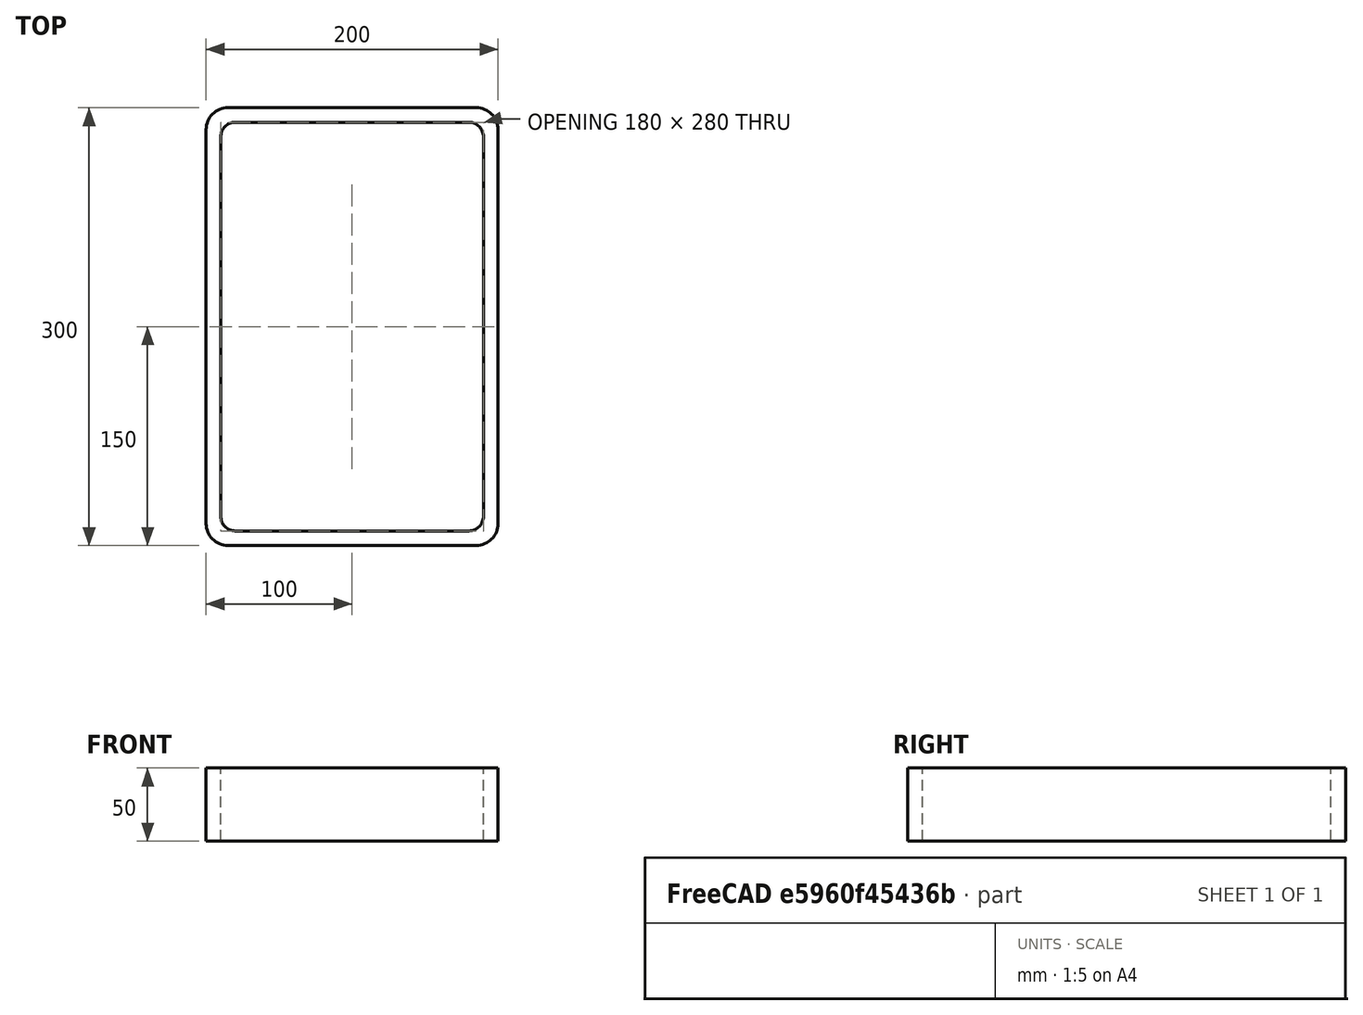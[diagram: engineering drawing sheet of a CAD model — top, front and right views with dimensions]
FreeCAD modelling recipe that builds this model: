
FCSTD DOCUMENT  (FreeCAD 0.15R4671 (Git))
Label: Rectangular hollow section 300x200x10 EN10219 S235JRH
License: All rights reserved
LicenseURL: http://en.wikipedia.org/wiki/All_rights_reserved
objects: Sketcher::SketchObject×1, Part::Extrusion×1
note: 2 computed .brp shape members not serialized (recipe doc carries the construction recipe); baked Part::Feature solids carry a one-line shape summary decoded from their .brp

FEATURE [Sketcher::SketchObject] Sketch
  sketch-geometry (16):
    g0: LineSegment StartX=-80 StartY=140 StartZ=0 EndX=80 EndY=140 EndZ=0
    g1: LineSegment StartX=90 StartY=130 StartZ=0 EndX=90 EndY=-130 EndZ=0
    g2: LineSegment StartX=80 StartY=-140 StartZ=0 EndX=-80 EndY=-140 EndZ=0
    g3: LineSegment StartX=-90 StartY=-130 StartZ=0 EndX=-90 EndY=130 EndZ=0
    g4: LineSegment StartX=-85 StartY=150 StartZ=0 EndX=85 EndY=150 EndZ=0
    g5: LineSegment StartX=100 StartY=135 StartZ=0 EndX=100 EndY=-135 EndZ=0
    g6: LineSegment StartX=85 StartY=-150 StartZ=0 EndX=-85 EndY=-150 EndZ=0
    g7: LineSegment StartX=-100 StartY=-135 StartZ=0 EndX=-100 EndY=135 EndZ=0
    g8: ArcOfCircle CenterX=-80 CenterY=130 CenterZ=0 NormalX=0 NormalY=0 NormalZ=1 Radius=10 StartAngle=1.5708 EndAngle=3.14159
    g9: ArcOfCircle CenterX=80 CenterY=130 CenterZ=0 NormalX=0 NormalY=0 NormalZ=1 Radius=10 StartAngle=0 EndAngle=1.5708
    g10: ArcOfCircle CenterX=80 CenterY=-130 CenterZ=0 NormalX=0 NormalY=0 NormalZ=1 Radius=10 StartAngle=4.71239 EndAngle=6.28319
    g11: ArcOfCircle CenterX=-80 CenterY=-130 CenterZ=0 NormalX=0 NormalY=0 NormalZ=1 Radius=10 StartAngle=3.14159 EndAngle=4.71239
    g12: ArcOfCircle CenterX=85 CenterY=135 CenterZ=0 NormalX=0 NormalY=0 NormalZ=1 Radius=15 StartAngle=0 EndAngle=1.5708
    g13: ArcOfCircle CenterX=85 CenterY=-135 CenterZ=0 NormalX=0 NormalY=0 NormalZ=1 Radius=15 StartAngle=4.71239 EndAngle=6.28319
    g14: ArcOfCircle CenterX=-85 CenterY=-135 CenterZ=0 NormalX=0 NormalY=0 NormalZ=1 Radius=15 StartAngle=3.14159 EndAngle=4.71239
    g15: ArcOfCircle CenterX=-85 CenterY=135 CenterZ=0 NormalX=0 NormalY=0 NormalZ=1 Radius=15 StartAngle=1.5708 EndAngle=3.14159
  constraints (36):
    c: Horizontal(g2)
    c: Vertical(g3)
    c: Horizontal(g6)
    c: Vertical(g7)
    c: Tangent(g3,g8) = 1.5708
    c: Tangent(g0,g8) = 1.5708
    c: Tangent(g0,g9) = 1.5708
    c: Tangent(g1,g9) = 1.5708
    c: Tangent(g1,g10) = 1.5708
    c: Tangent(g2,g10) = 1.5708
    c: Tangent(g2,g11) = 1.5708
    c: Tangent(g3,g11) = 1.5708
    c: Tangent(g4,g12) = 1.5708
    c: Tangent(g5,g12) = 1.5708
    c: Tangent(g5,g13) = 1.5708
    c: Tangent(g6,g13) = 1.5708
    c: Tangent(g6,g14) = 1.5708
    c: Tangent(g7,g14) = 1.5708
    c: Tangent(g7,g15) = 1.5708
    c: Tangent(g4,g15) = 1.5708
    c: Equal(g9,g8)
    c: Equal(g9,g11)
    c: Equal(g9,g10)
    c: Equal(g12,g15)
    c: Equal(g12,g14)
    c: Equal(g12,g13)
    c: Symmetric(g4,g6,g-1)
    c: Symmetric(g7,g5,g-2)
    c: DistanceY(g4,g6) = -300
    c: DistanceX(g7,g5) = 200
    c: Symmetric(g3,g1,g-2)
    c: Symmetric(g0,g2,g-1)
    c: DistanceY(g0,g4) = 10
    c: DistanceX(g5,g1) = -10
    c: Radius(g9) = 10
    c: Radius(g12) = 15
FEATURE [Part::Extrusion] Extrude  label="Rectangular hollow section 300x200x10 EN10219 S235JRH"
  Base = -> Sketch
  Dir = (0,0,50)
  Solid = true
